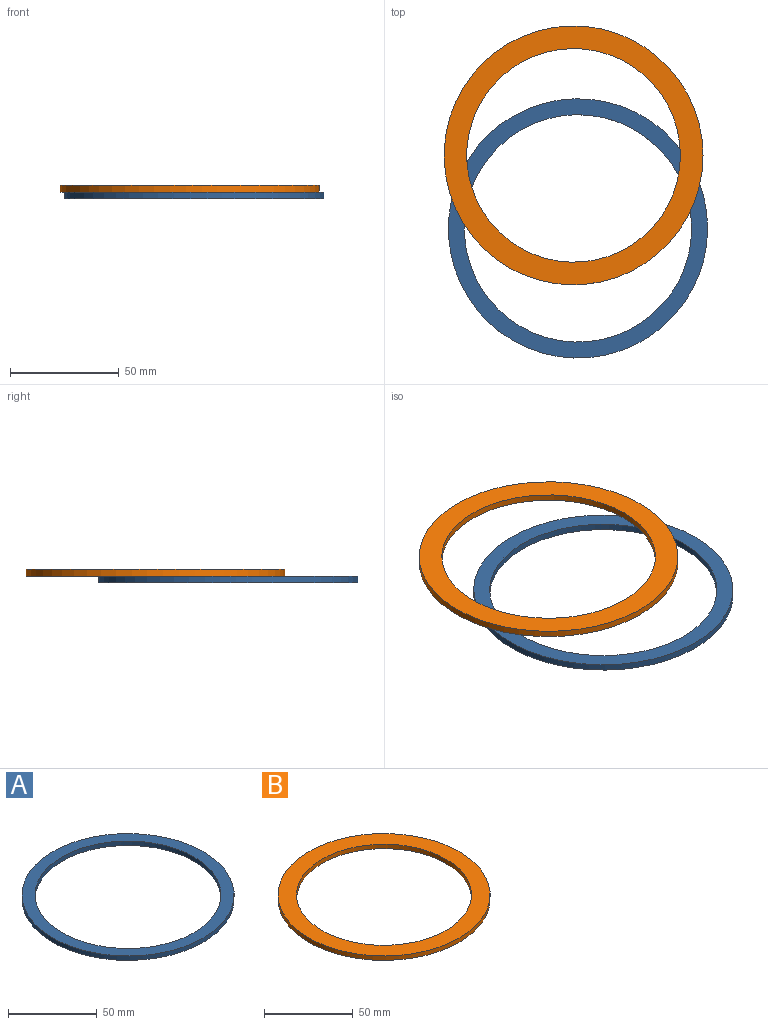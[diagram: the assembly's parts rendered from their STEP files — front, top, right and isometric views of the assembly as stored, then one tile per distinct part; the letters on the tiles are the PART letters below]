
ASSEMBLY  parts=2 mates=1
PART A: 4 faces, bbox 119.4x119.4x3 mm
  f0: cylinder r=52.33mm len=104.67mm, axis (0,0,-1), area 986.5mm2, adj f2,f3
  f1: cylinder r=59.68mm len=119.35mm, axis (0,0,-1), area 1124.9mm2, adj f2,f3
  f2: plane 119.35x119.35mm, normal (0,0,1), area 2583.7mm2, adj f0,f1
  f3: plane 119.35x119.35mm, normal (0,0,-1), area 2583.7mm2, adj f0,f1
PART B: 4 faces, bbox 119.2x119.2x3 mm
  f0: cylinder r=49.16mm len=98.32mm, axis (0,0,-1), area 926.7mm2, adj f2,f3
  f1: cylinder r=59.59mm len=119.17mm, axis (0,0,-1), area 1123.2mm2, adj f2,f3
  f2: plane 119.17x119.17mm, normal (0,0,1), area 3561.9mm2, adj f0,f1
  f3: plane 119.17x119.17mm, normal (0,0,-1), area 3561.9mm2, adj f0,f1
PLACE A t=(28.88,-28.59,24.01)mm
PLACE B t=(26.87,5.01,27.01)mm
MATE planar B.f0 <-> A.f0  axis (0,0,-1) through (26.87,5.01,27.01)mm
